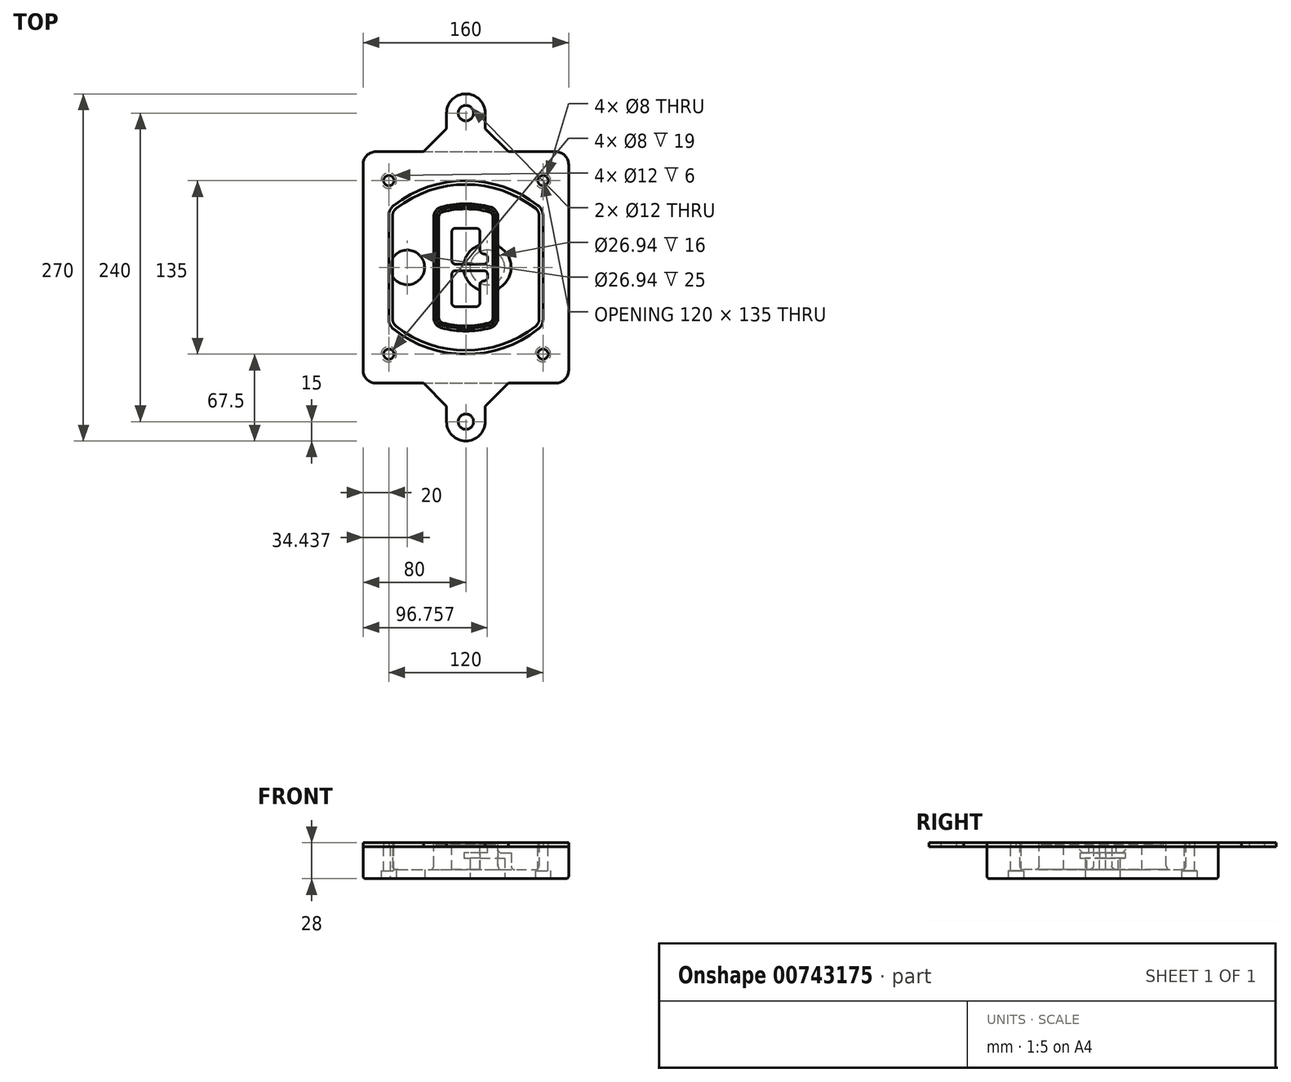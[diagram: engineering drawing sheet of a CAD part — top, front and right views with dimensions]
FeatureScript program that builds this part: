
annotation { "Feature Type Name" : "Feature", "Feature Type Description" : "" }
export const myFeature = defineFeature(function(context is Context, id is Id, definition is map)
    precondition{}
    {
        {
            var Q0;
            Q0=qCreatedBy(makeId("Top.planeOp"),FACE);
            var sketch = newSketch(context, id + "F0", { "sketchPlane" : qUnion([Q0])});
            skPoint(sketch, "E0.rect.middle", {"position": v(0, 0) * mm});
            skLineSegment(sketch, "E1.bottom", {"start": v(-70, -90) * mm, "end": v(70, -90) * mm});
            skLineSegment(sketch, "E1.top", {"start": v(-70, 90) * mm, "end": v(70, 90) * mm});
            skLineSegment(sketch, "E1.left", {"start": v(-80, -80) * mm, "end": v(-80, 80) * mm});
            skLineSegment(sketch, "E1.right", {"start": v(80, -80) * mm, "end": v(80, 80) * mm});
            skLineSegment(sketch, "E2", {"start": v(-80, 90) * mm, "end": v(80, -90) * mm, "construction": true});
            skLineSegment(sketch, "E3", {"start": v(80, 90) * mm, "end": v(-80, -90) * mm, "construction": true});
            skCircle(sketch, "E4", {"center": v(-60, 67.5) * mm, "radius": 4 * mm});
            skCircle(sketch, "E5", {"center": v(60, 67.5) * mm, "radius": 4 * mm});
            skCircle(sketch, "E6", {"center": v(60, -67.5) * mm, "radius": 4 * mm});
            skCircle(sketch, "E7", {"center": v(-60, -67.5) * mm, "radius": 4 * mm});
            skLineSegment(sketch, "E8", {"start": v(-60, 67.5) * mm, "end": v(60, 67.5) * mm, "construction": true});
            skLineSegment(sketch, "E9", {"start": v(60, 67.5) * mm, "end": v(60, -67.5) * mm, "construction": true});
            skLineSegment(sketch, "E10", {"start": v(60, -67.5) * mm, "end": v(-60, -67.5) * mm, "construction": true});
            skLineSegment(sketch, "E11", {"start": v(-60, -67.5) * mm, "end": v(-60, 67.5) * mm, "construction": true});
            skLineSegment(sketch, "E12", {"start": v(-60, 40.3) * mm, "end": v(-60, -40.3) * mm});
            skLineSegment(sketch, "E13", {"start": v(60, 40.3) * mm, "end": v(60, -40.3) * mm});
            skArc(sketch, "E14", {"start": v(56.15, 48.18) * mm, "mid": v(0, 67.5) * mm, "end": v(-56.15, 48.18) * mm});
            skArc(sketch, "E15", {"start": v(-56.15, -48.18) * mm, "mid": v(0, -67.5) * mm, "end": v(56.15, -48.18) * mm});
            skLineSegment(sketch, "E16", {"start": v(-60, 0) * mm, "end": v(60, 0) * mm, "construction": true});
            skPoint(sketch, "E17.visualSharp", {"position": v(-60, -45) * mm});
            skArc(sketch, "E17.filletArc", {"start": v(-60, -40.3) * mm, "mid": v(-58.99, -44.68) * mm, "end": v(-56.15, -48.18) * mm});
            skPoint(sketch, "E18.visualSharp", {"position": v(-60, 45) * mm});
            skArc(sketch, "E18.filletArc", {"start": v(-56.15, 48.18) * mm, "mid": v(-58.99, 44.68) * mm, "end": v(-60, 40.3) * mm});
            skPoint(sketch, "E19.visualSharp", {"position": v(60, 45) * mm});
            skArc(sketch, "E19.filletArc", {"start": v(60, 40.3) * mm, "mid": v(58.99, 44.68) * mm, "end": v(56.15, 48.18) * mm});
            skPoint(sketch, "E20.visualSharp", {"position": v(60, -45) * mm});
            skArc(sketch, "E20.filletArc", {"start": v(56.15, -48.18) * mm, "mid": v(58.99, -44.68) * mm, "end": v(60, -40.3) * mm});
            skPoint(sketch, "E21.visualSharp", {"position": v(-80, 90) * mm});
            skArc(sketch, "E21.filletArc", {"start": v(-70, 90) * mm, "mid": v(-77.07, 87.07) * mm, "end": v(-80, 80) * mm});
            skPoint(sketch, "E22.visualSharp", {"position": v(80, 90) * mm});
            skArc(sketch, "E22.filletArc", {"start": v(80, 80) * mm, "mid": v(77.07, 87.07) * mm, "end": v(70, 90) * mm});
            skPoint(sketch, "E23.visualSharp", {"position": v(80, -90) * mm});
            skArc(sketch, "E23.filletArc", {"start": v(70, -90) * mm, "mid": v(77.07, -87.07) * mm, "end": v(80, -80) * mm});
            skPoint(sketch, "E24.visualSharp", {"position": v(-80, -90) * mm});
            skArc(sketch, "E24.filletArc", {"start": v(-80, -80) * mm, "mid": v(-77.07, -87.07) * mm, "end": v(-70, -90) * mm});
            skArc(sketch, "E25.0", {"start": v(57, 40.3) * mm, "mid": v(56.3, 43.36) * mm, "end": v(54.3, 45.81) * mm});
            skLineSegment(sketch, "E25.1", {"start": v(57, 40.3) * mm, "end": v(57, -40.3) * mm});
            skArc(sketch, "E25.2", {"start": v(54.3, -45.81) * mm, "mid": v(56.3, -43.36) * mm, "end": v(57, -40.3) * mm});
            skArc(sketch, "E25.3", {"start": v(-54.3, -45.81) * mm, "mid": v(0, -64.5) * mm, "end": v(54.3, -45.81) * mm});
            skArc(sketch, "E25.4", {"start": v(-57, -40.3) * mm, "mid": v(-56.3, -43.36) * mm, "end": v(-54.3, -45.81) * mm});
            skArc(sketch, "E25.5", {"start": v(54.3, 45.81) * mm, "mid": v(0, 64.5) * mm, "end": v(-54.3, 45.81) * mm});
            skLineSegment(sketch, "E25.6", {"start": v(-57, 40.3) * mm, "end": v(-57, -40.3) * mm});
            skArc(sketch, "E25.7", {"start": v(-54.3, 45.81) * mm, "mid": v(-56.3, 43.36) * mm, "end": v(-57, 40.3) * mm});
            skArc(sketch, "E26.0", {"start": v(-58.62, 51.33) * mm, "mid": v(-62.58, 46.43) * mm, "end": v(-64, 40.3) * mm});
            skArc(sketch, "E26.1", {"start": v(58.62, 51.33) * mm, "mid": v(0, 71.5) * mm, "end": v(-58.62, 51.33) * mm});
            skArc(sketch, "E26.2", {"start": v(64, 40.3) * mm, "mid": v(62.58, 46.43) * mm, "end": v(58.62, 51.33) * mm});
            skLineSegment(sketch, "E26.3", {"start": v(64, 40.3) * mm, "end": v(64, -40.3) * mm});
            skArc(sketch, "E26.4", {"start": v(58.62, -51.33) * mm, "mid": v(62.58, -46.43) * mm, "end": v(64, -40.3) * mm});
            skLineSegment(sketch, "E26.5", {"start": v(-64, 40.3) * mm, "end": v(-64, -40.3) * mm});
            skArc(sketch, "E26.6", {"start": v(-58.62, -51.33) * mm, "mid": v(0, -71.5) * mm, "end": v(58.62, -51.33) * mm});
            skArc(sketch, "E26.7", {"start": v(-64, -40.3) * mm, "mid": v(-62.58, -46.43) * mm, "end": v(-58.62, -51.33) * mm});
            skSolve(sketch);
        }
        {
            var Q0;
            Q0=makeQuery(id+"F0.imprint","IMPRINT",FACE,{"disambiguationData":[TD([[makeQuery(id+"F0.imprint","IMPRINT",EDGE,{"derivedFrom":sQuery(id+"F0.wireOp",EDGE,"E1.bottom")}),1.0]])]});
            var Q1;
            Q1=makeQuery(id+"F0.imprint","IMPRINT",FACE,{"disambiguationData":[TD([[makeQuery(id+"F0.imprint","IMPRINT",EDGE,{"derivedFrom":sQuery(id+"F0.wireOp",EDGE,"E12")}),1.0]])]});
            var Q2;
            Q2=makeQuery(id+"F0.imprint","IMPRINT",FACE,{"disambiguationData":[TD([[makeQuery(id+"F0.imprint","IMPRINT",EDGE,{"derivedFrom":sQuery(id+"F0.wireOp",EDGE,"E25.0")}),1.0]])]});
            var Q3;
            Q3=makeQuery(id+"F0.imprint","IMPRINT",FACE,{"disambiguationData":[TD([[makeQuery(id+"F0.imprint","IMPRINT",EDGE,{"derivedFrom":sQuery(id+"F0.wireOp",EDGE,"E12")}),-1.0]])]});
            extrude(context, id + "F1", {"entities" : qUnion([Q0, Q1, Q2, Q3]), "oppositeDirection" : true, "depth" : 25 * mm});
        }
        {
            var Q0;
            Q0=makeQuery(id+"F0.imprint","IMPRINT",FACE,{"disambiguationData":[TD([[makeQuery(id+"F0.imprint","IMPRINT",EDGE,{"derivedFrom":sQuery(id+"F0.wireOp",EDGE,"E12")}),1.0]])]});
            extrude(context, id + "F2", {"entities" : qUnion([Q0]), "operationType" : NewBodyOperationType.ADD, "depth" : 3 * mm});
        }
        {
            var Q0;
            Q0=makeQuery(id+"F0.imprint","IMPRINT",FACE,{"disambiguationData":[TD([[makeQuery(id+"F0.imprint","IMPRINT",EDGE,{"derivedFrom":sQuery(id+"F0.wireOp",EDGE,"E25.0")}),1.0]])]});
            extrude(context, id + "F3", {"entities" : qUnion([Q0]), "operationType" : NewBodyOperationType.REMOVE, "oppositeDirection" : true, "depth" : 18 * mm});
        }
        {
            var Q0;
            Q0=makeQuery(id+"F2.opExtrude","CAP_FACE",FACE,{"disambiguationData":[OSD([sQuery(id+"F0.wireOp",EDGE,"E12"),sQuery(id+"F0.wireOp",EDGE,"E13"),sQuery(id+"F0.wireOp",EDGE,"E14"),sQuery(id+"F0.wireOp",EDGE,"E15"),sQuery(id+"F0.wireOp",EDGE,"E17.filletArc"),sQuery(id+"F0.wireOp",EDGE,"E18.filletArc"),sQuery(id+"F0.wireOp",EDGE,"E19.filletArc"),sQuery(id+"F0.wireOp",EDGE,"E20.filletArc"),sQuery(id+"F0.wireOp",EDGE,"E25.0"),sQuery(id+"F0.wireOp",EDGE,"E25.1"),sQuery(id+"F0.wireOp",EDGE,"E25.2"),sQuery(id+"F0.wireOp",EDGE,"E25.3"),sQuery(id+"F0.wireOp",EDGE,"E25.4"),sQuery(id+"F0.wireOp",EDGE,"E25.5"),sQuery(id+"F0.wireOp",EDGE,"E25.6"),sQuery(id+"F0.wireOp",EDGE,"E25.7")])],"isStart":false});
            var sketch = newSketch(context, id + "F4", { "sketchPlane" : qUnion([Q0])});
            skArc(sketch, "E27.0", {"start": v(-19.08, -46.97) * mm, "mid": v(0, -49.5) * mm, "end": v(19.08, -46.97) * mm});
            skArc(sketch, "E28.0", {"start": v(19.08, 46.97) * mm, "mid": v(0, 49.5) * mm, "end": v(-19.08, 46.97) * mm});
            skLineSegment(sketch, "E29", {"start": v(-25, 39.25) * mm, "end": v(-25, -39.25) * mm});
            skLineSegment(sketch, "E30", {"start": v(25, 39.25) * mm, "end": v(25, -39.25) * mm});
            skLineSegment(sketch, "E31", {"start": v(-25, 45.1) * mm, "end": v(25, 45.1) * mm, "construction": true});
            skLineSegment(sketch, "E32", {"start": v(-25, -45.1) * mm, "end": v(25, -45.1) * mm, "construction": true});
            skPoint(sketch, "E33.visualSharp", {"position": v(-25, 45.1) * mm});
            skArc(sketch, "E33.filletArc", {"start": v(-19.08, 46.97) * mm, "mid": v(-23.35, 44.11) * mm, "end": v(-25, 39.25) * mm});
            skPoint(sketch, "E34.visualSharp", {"position": v(25, 45.1) * mm});
            skArc(sketch, "E34.filletArc", {"start": v(25, 39.25) * mm, "mid": v(23.35, 44.11) * mm, "end": v(19.08, 46.97) * mm});
            skPoint(sketch, "E35.visualSharp", {"position": v(25, -45.1) * mm});
            skArc(sketch, "E35.filletArc", {"start": v(19.08, -46.97) * mm, "mid": v(23.35, -44.11) * mm, "end": v(25, -39.25) * mm});
            skPoint(sketch, "E36.visualSharp", {"position": v(-25, -45.1) * mm});
            skArc(sketch, "E36.filletArc", {"start": v(-25, -39.25) * mm, "mid": v(-23.35, -44.11) * mm, "end": v(-19.08, -46.97) * mm});
            skArc(sketch, "E37.0", {"start": v(54.3, 45.81) * mm, "mid": v(0, 64.5) * mm, "end": v(-54.3, 45.81) * mm});
            skArc(sketch, "E37.1", {"start": v(-54.3, 45.81) * mm, "mid": v(-56.3, 43.36) * mm, "end": v(-57, 40.3) * mm});
            skLineSegment(sketch, "E37.2", {"start": v(-57, 40.3) * mm, "end": v(-57, -40.3) * mm});
            skArc(sketch, "E37.3", {"start": v(-57, -40.3) * mm, "mid": v(-56.3, -43.36) * mm, "end": v(-54.3, -45.81) * mm});
            skArc(sketch, "E37.4", {"start": v(-54.3, -45.81) * mm, "mid": v(0, -64.5) * mm, "end": v(54.3, -45.81) * mm});
            skArc(sketch, "E37.5", {"start": v(54.3, -45.81) * mm, "mid": v(56.3, -43.36) * mm, "end": v(57, -40.3) * mm});
            skLineSegment(sketch, "E37.6", {"start": v(57, 40.3) * mm, "end": v(57, -40.3) * mm});
            skArc(sketch, "E37.7", {"start": v(57, 40.3) * mm, "mid": v(56.3, 43.36) * mm, "end": v(54.3, 45.81) * mm});
            skLineSegment(sketch, "E38.0", {"start": v(23, 39.25) * mm, "end": v(23, -39.25) * mm});
            skArc(sketch, "E38.1", {"start": v(18.56, -45.04) * mm, "mid": v(21.76, -42.9) * mm, "end": v(23, -39.25) * mm});
            skArc(sketch, "E38.2", {"start": v(-18.56, -45.04) * mm, "mid": v(0, -47.5) * mm, "end": v(18.56, -45.04) * mm});
            skArc(sketch, "E38.3", {"start": v(-23, -39.25) * mm, "mid": v(-21.76, -42.9) * mm, "end": v(-18.56, -45.04) * mm});
            skLineSegment(sketch, "E38.4", {"start": v(-23, 39.25) * mm, "end": v(-23, -39.25) * mm});
            skArc(sketch, "E38.5", {"start": v(23, 39.25) * mm, "mid": v(21.76, 42.9) * mm, "end": v(18.56, 45.04) * mm});
            skArc(sketch, "E38.6", {"start": v(-18.56, 45.04) * mm, "mid": v(-21.76, 42.9) * mm, "end": v(-23, 39.25) * mm});
            skArc(sketch, "E38.7", {"start": v(18.56, 45.04) * mm, "mid": v(0, 47.5) * mm, "end": v(-18.56, 45.04) * mm});
            skArc(sketch, "E39.0", {"start": v(21, 39.25) * mm, "mid": v(20.18, 41.68) * mm, "end": v(18.04, 43.1) * mm});
            skLineSegment(sketch, "E39.1", {"start": v(21, 39.25) * mm, "end": v(21, -39.25) * mm});
            skArc(sketch, "E39.2", {"start": v(18.04, -43.1) * mm, "mid": v(20.18, -41.68) * mm, "end": v(21, -39.25) * mm});
            skArc(sketch, "E39.3", {"start": v(-18.04, -43.1) * mm, "mid": v(0, -45.5) * mm, "end": v(18.04, -43.1) * mm});
            skArc(sketch, "E39.4", {"start": v(-21, -39.25) * mm, "mid": v(-20.18, -41.68) * mm, "end": v(-18.04, -43.1) * mm});
            skArc(sketch, "E39.5", {"start": v(18.04, 43.1) * mm, "mid": v(0, 45.5) * mm, "end": v(-18.04, 43.1) * mm});
            skLineSegment(sketch, "E39.6", {"start": v(-21, 39.25) * mm, "end": v(-21, -39.25) * mm});
            skArc(sketch, "E39.7", {"start": v(-18.04, 43.1) * mm, "mid": v(-20.18, 41.68) * mm, "end": v(-21, 39.25) * mm});
            skLineSegment(sketch, "E40", {"start": v(-25, 0) * mm, "end": v(25, 0) * mm, "construction": true});
            skLineSegment(sketch, "E41", {"start": v(-11, 5.5) * mm, "end": v(-11, 27.5) * mm});
            skLineSegment(sketch, "E42", {"start": v(-8, 30.5) * mm, "end": v(8, 30.5) * mm});
            skLineSegment(sketch, "E43", {"start": v(11, 27.5) * mm, "end": v(11, 13.5) * mm});
            skLineSegment(sketch, "E44", {"start": v(14, 10.5) * mm, "end": v(14, 10.5) * mm});
            skLineSegment(sketch, "E45", {"start": v(17, 7.5) * mm, "end": v(17, 5.5) * mm});
            skLineSegment(sketch, "E46", {"start": v(14, 2.5) * mm, "end": v(-8, 2.5) * mm});
            skPoint(sketch, "E47.visualSharp", {"position": v(-11, 30.5) * mm});
            skArc(sketch, "E47.filletArc", {"start": v(-8, 30.5) * mm, "mid": v(-10.12, 29.62) * mm, "end": v(-11, 27.5) * mm});
            skPoint(sketch, "E48.visualSharp", {"position": v(11, 30.5) * mm});
            skArc(sketch, "E48.filletArc", {"start": v(11, 27.5) * mm, "mid": v(10.12, 29.62) * mm, "end": v(8, 30.5) * mm});
            skPoint(sketch, "E49.visualSharp", {"position": v(11, 10.5) * mm});
            skArc(sketch, "E49.filletArc", {"start": v(11, 13.5) * mm, "mid": v(11.88, 11.38) * mm, "end": v(14, 10.5) * mm});
            skPoint(sketch, "E50.visualSharp", {"position": v(17, 10.5) * mm});
            skArc(sketch, "E50.filletArc", {"start": v(17, 7.5) * mm, "mid": v(16.12, 9.62) * mm, "end": v(14, 10.5) * mm});
            skPoint(sketch, "E51.visualSharp", {"position": v(17, 2.5) * mm});
            skArc(sketch, "E51.filletArc", {"start": v(14, 2.5) * mm, "mid": v(16.12, 3.38) * mm, "end": v(17, 5.5) * mm});
            skPoint(sketch, "E52.visualSharp", {"position": v(-11, 2.5) * mm});
            skArc(sketch, "E52.filletArc", {"start": v(-11, 5.5) * mm, "mid": v(-10.12, 3.38) * mm, "end": v(-8, 2.5) * mm});
            skLineSegment(sketch, "E53.0.MirrorCS", {"start": v(14, -2.5) * mm, "end": v(-8, -2.5) * mm});
            skArc(sketch, "E54.0.MirrorCS", {"start": v(-11, -5.5) * mm, "mid": v(-10.12, -3.38) * mm, "end": v(-8, -2.5) * mm});
            skLineSegment(sketch, "E55.0.MirrorCS", {"start": v(-11, -5.5) * mm, "end": v(-11, -27.5) * mm});
            skArc(sketch, "E56.0.MirrorCS", {"start": v(-8, -30.5) * mm, "mid": v(-10.12, -29.62) * mm, "end": v(-11, -27.5) * mm});
            skLineSegment(sketch, "E57.0.MirrorCS", {"start": v(-8, -30.5) * mm, "end": v(8, -30.5) * mm});
            skArc(sketch, "E58.0.MirrorCS", {"start": v(11, -27.5) * mm, "mid": v(10.12, -29.62) * mm, "end": v(8, -30.5) * mm});
            skLineSegment(sketch, "E59.0.MirrorCS", {"start": v(11, -27.5) * mm, "end": v(11, -13.5) * mm});
            skArc(sketch, "E60.0.MirrorCS", {"start": v(11, -13.5) * mm, "mid": v(11.88, -11.38) * mm, "end": v(14, -10.5) * mm});
            skArc(sketch, "E61.0.MirrorCS", {"start": v(17, -7.5) * mm, "mid": v(16.12, -9.62) * mm, "end": v(14, -10.5) * mm});
            skLineSegment(sketch, "E62.0.MirrorCS", {"start": v(17, -7.5) * mm, "end": v(17, -5.5) * mm});
            skArc(sketch, "E63.0.MirrorCS", {"start": v(14, -2.5) * mm, "mid": v(16.12, -3.38) * mm, "end": v(17, -5.5) * mm});
            skSolve(sketch);
        }
        {
            var Q0;
            Q0=makeQuery(id+"F4.imprint","IMPRINT",FACE,{"disambiguationData":[TD([[makeQuery(id+"F4.imprint","IMPRINT",EDGE,{"derivedFrom":sQuery(id+"F4.wireOp",EDGE,"E27.0")}),1.0]])]});
            var Q1;
            Q1=makeQuery(id+"F4.imprint","IMPRINT",FACE,{"disambiguationData":[TD([[makeQuery(id+"F4.imprint","IMPRINT",EDGE,{"derivedFrom":sQuery(id+"F4.wireOp",EDGE,"E38.0")}),-1.0]])]});
            var Q2;
            Q2=makeQuery(id+"F4.imprint","IMPRINT",FACE,{"disambiguationData":[TD([[makeQuery(id+"F4.imprint","IMPRINT",EDGE,{"derivedFrom":sQuery(id+"F4.wireOp",EDGE,"E39.0")}),1.0]])]});
            extrude(context, id + "F5", {"entities" : qUnion([Q0, Q1, Q2]), "operationType" : NewBodyOperationType.ADD, "endBound" : BoundingType.UP_TO_NEXT, "oppositeDirection" : true, "depth" : 25 * mm});
        }
        {
            var Q0;
            Q0=makeQuery(id+"F4.imprint","IMPRINT",FACE,{"disambiguationData":[TD([[makeQuery(id+"F4.imprint","IMPRINT",EDGE,{"derivedFrom":sQuery(id+"F4.wireOp",EDGE,"E38.0")}),-1.0]])]});
            extrude(context, id + "F6", {"entities" : qUnion([Q0]), "operationType" : NewBodyOperationType.REMOVE, "oppositeDirection" : true, "depth" : 2 * mm});
        }
        {
            var Q0;
            Q0=makeQuery(id+"F1.opExtrude","CAP_FACE",FACE,{"disambiguationData":[OSD([sQuery(id+"F0.wireOp",EDGE,"E1.bottom"),sQuery(id+"F0.wireOp",EDGE,"E1.top"),sQuery(id+"F0.wireOp",EDGE,"E1.left"),sQuery(id+"F0.wireOp",EDGE,"E1.right"),sQuery(id+"F0.wireOp",EDGE,"E4"),sQuery(id+"F0.wireOp",EDGE,"E5"),sQuery(id+"F0.wireOp",EDGE,"E6"),sQuery(id+"F0.wireOp",EDGE,"E7"),sQuery(id+"F0.wireOp",EDGE,"E21.filletArc"),sQuery(id+"F0.wireOp",EDGE,"E22.filletArc"),sQuery(id+"F0.wireOp",EDGE,"E23.filletArc"),sQuery(id+"F0.wireOp",EDGE,"E24.filletArc")])],"isStart":false});
            var sketch = newSketch(context, id + "F7", { "sketchPlane" : qUnion([Q0])});
            skCircle(sketch, "E64", {"center": v(16.76, 0) * mm, "radius": 13.47 * mm});
            skCircle(sketch, "E65", {"center": v(-45.56, 0) * mm, "radius": 13.47 * mm});
            skLineSegment(sketch, "E66", {"start": v(80, 0) * mm, "end": v(-80, 0) * mm});
            skCircle(sketch, "E67", {"center": v(16.76, 0) * mm, "radius": 18.47 * mm});
            skCircle(sketch, "E68", {"center": v(60, -67.5) * mm, "radius": 6 * mm});
            skCircle(sketch, "E69", {"center": v(-60, -67.5) * mm, "radius": 6 * mm});
            skCircle(sketch, "E70", {"center": v(-60, 67.5) * mm, "radius": 6 * mm});
            skCircle(sketch, "E71", {"center": v(60, 67.5) * mm, "radius": 6 * mm});
            skSolve(sketch);
        }
        {
            var Q0;
            {var subQ1=sQuery(id+"F7.wireOp",EDGE,"E66");var subQ4=sQuery(id+"F7.wireOp",EDGE,"E64");var subQ6=makeQuery(id+"F7.imprint","INTERSECT",VERTEX,{"disambiguationData":[OD(0.0)],"derivedFrom":[subQ4,subQ1]});Q0=makeQuery(id+"F7.imprint","IMPRINT",FACE,{"disambiguationData":[TD([[makeQuery(id+"F7.imprint","IMPRINT",EDGE,{"disambiguationData":[TD([[subQ6,-1.0]])],"derivedFrom":subQ4}),-1.0]])]});}
            var Q1;
            {var subQ0=sQuery(id+"F7.wireOp",EDGE,"E66");var subQ1=sQuery(id+"F7.wireOp",EDGE,"E64");var subQ3=makeQuery(id+"F7.imprint","INTERSECT",VERTEX,{"disambiguationData":[OD(0.0)],"derivedFrom":[subQ1,subQ0]});Q1=makeQuery(id+"F7.imprint","IMPRINT",FACE,{"disambiguationData":[TD([[makeQuery(id+"F7.imprint","IMPRINT",EDGE,{"disambiguationData":[TD([[subQ3,-1.0]])],"derivedFrom":subQ1}),1.0]])]});}
            var Q2;
            {var subQ0=sQuery(id+"F7.wireOp",EDGE,"E66");var subQ1=sQuery(id+"F7.wireOp",EDGE,"E64");var subQ3=makeQuery(id+"F7.imprint","INTERSECT",VERTEX,{"disambiguationData":[OD(0.0)],"derivedFrom":[subQ1,subQ0]});Q2=makeQuery(id+"F7.imprint","IMPRINT",FACE,{"disambiguationData":[TD([[makeQuery(id+"F7.imprint","IMPRINT",EDGE,{"disambiguationData":[TD([[subQ3,1.0]])],"derivedFrom":subQ1}),1.0]])]});}
            var Q3;
            {var subQ1=sQuery(id+"F7.wireOp",EDGE,"E66");var subQ4=sQuery(id+"F7.wireOp",EDGE,"E64");var subQ6=makeQuery(id+"F7.imprint","INTERSECT",VERTEX,{"disambiguationData":[OD(0.0)],"derivedFrom":[subQ4,subQ1]});Q3=makeQuery(id+"F7.imprint","IMPRINT",FACE,{"disambiguationData":[TD([[makeQuery(id+"F7.imprint","IMPRINT",EDGE,{"disambiguationData":[TD([[subQ6,1.0]])],"derivedFrom":subQ4}),-1.0]])]});}
            extrude(context, id + "F8", {"entities" : qUnion([Q0, Q1, Q2, Q3]), "operationType" : NewBodyOperationType.ADD, "oppositeDirection" : true, "depth" : 20 * mm});
        }
        {
            var Q0;
            {var subQ0=sQuery(id+"F7.wireOp",EDGE,"E66");var subQ1=sQuery(id+"F7.wireOp",EDGE,"E64");var subQ3=makeQuery(id+"F7.imprint","INTERSECT",VERTEX,{"disambiguationData":[OD(0.0)],"derivedFrom":[subQ1,subQ0]});Q0=makeQuery(id+"F7.imprint","IMPRINT",FACE,{"disambiguationData":[TD([[makeQuery(id+"F7.imprint","IMPRINT",EDGE,{"disambiguationData":[TD([[subQ3,-1.0]])],"derivedFrom":subQ1}),1.0]])]});}
            var Q1;
            {var subQ0=sQuery(id+"F7.wireOp",EDGE,"E66");var subQ1=sQuery(id+"F7.wireOp",EDGE,"E64");var subQ3=makeQuery(id+"F7.imprint","INTERSECT",VERTEX,{"disambiguationData":[OD(0.0)],"derivedFrom":[subQ1,subQ0]});Q1=makeQuery(id+"F7.imprint","IMPRINT",FACE,{"disambiguationData":[TD([[makeQuery(id+"F7.imprint","IMPRINT",EDGE,{"disambiguationData":[TD([[subQ3,1.0]])],"derivedFrom":subQ1}),1.0]])]});}
            extrude(context, id + "F9", {"entities" : qUnion([Q0, Q1]), "operationType" : NewBodyOperationType.REMOVE, "oppositeDirection" : true, "depth" : 16 * mm});
        }
        {
            var Q0;
            {var subQ0=sQuery(id+"F7.wireOp",EDGE,"E66");var subQ1=sQuery(id+"F7.wireOp",EDGE,"E65");var subQ3=makeQuery(id+"F7.imprint","INTERSECT",VERTEX,{"disambiguationData":[OD(0.0)],"derivedFrom":[subQ1,subQ0]});Q0=makeQuery(id+"F7.imprint","IMPRINT",FACE,{"disambiguationData":[TD([[makeQuery(id+"F7.imprint","IMPRINT",EDGE,{"disambiguationData":[TD([[subQ3,-1.0]])],"derivedFrom":subQ1}),1.0]])]});}
            var Q1;
            {var subQ0=sQuery(id+"F7.wireOp",EDGE,"E66");var subQ1=sQuery(id+"F7.wireOp",EDGE,"E65");var subQ3=makeQuery(id+"F7.imprint","INTERSECT",VERTEX,{"disambiguationData":[OD(0.0)],"derivedFrom":[subQ1,subQ0]});Q1=makeQuery(id+"F7.imprint","IMPRINT",FACE,{"disambiguationData":[TD([[makeQuery(id+"F7.imprint","IMPRINT",EDGE,{"disambiguationData":[TD([[subQ3,1.0]])],"derivedFrom":subQ1}),1.0]])]});}
            extrude(context, id + "F10", {"entities" : qUnion([Q0, Q1]), "operationType" : NewBodyOperationType.REMOVE, "oppositeDirection" : true, "depth" : 25 * mm});
        }
        {
            var Q0;
            Q0=makeQuery(id+"F7.imprint","IMPRINT",FACE,{"disambiguationData":[TD([[makeQuery(id+"F7.imprint","IMPRINT",EDGE,{"derivedFrom":sQuery(id+"F7.wireOp",EDGE,"E68")}),1.0]])]});
            var Q1;
            Q1=makeQuery(id+"F7.imprint","IMPRINT",FACE,{"disambiguationData":[TD([[makeQuery(id+"F7.imprint","IMPRINT",EDGE,{"derivedFrom":makeQuery(id+"F1.opExtrude","CAP_EDGE",EDGE,{"disambiguationData":[OSD([sQuery(id+"F0.wireOp",EDGE,"E5")])],"isStart":false})}),-1.0]])]});
            var Q2;
            Q2=makeQuery(id+"F7.imprint","IMPRINT",FACE,{"disambiguationData":[TD([[makeQuery(id+"F7.imprint","IMPRINT",EDGE,{"derivedFrom":sQuery(id+"F7.wireOp",EDGE,"E69")}),1.0]])]});
            var Q3;
            Q3=makeQuery(id+"F7.imprint","IMPRINT",FACE,{"disambiguationData":[TD([[makeQuery(id+"F7.imprint","IMPRINT",EDGE,{"derivedFrom":makeQuery(id+"F1.opExtrude","CAP_EDGE",EDGE,{"disambiguationData":[OSD([sQuery(id+"F0.wireOp",EDGE,"E4")])],"isStart":false})}),-1.0]])]});
            var Q4;
            Q4=makeQuery(id+"F7.imprint","IMPRINT",FACE,{"disambiguationData":[TD([[makeQuery(id+"F7.imprint","IMPRINT",EDGE,{"derivedFrom":sQuery(id+"F7.wireOp",EDGE,"E70")}),1.0]])]});
            var Q5;
            Q5=makeQuery(id+"F7.imprint","IMPRINT",FACE,{"disambiguationData":[TD([[makeQuery(id+"F7.imprint","IMPRINT",EDGE,{"derivedFrom":makeQuery(id+"F1.opExtrude","CAP_EDGE",EDGE,{"disambiguationData":[OSD([sQuery(id+"F0.wireOp",EDGE,"E7")])],"isStart":false})}),-1.0]])]});
            var Q6;
            Q6=makeQuery(id+"F7.imprint","IMPRINT",FACE,{"disambiguationData":[TD([[makeQuery(id+"F7.imprint","IMPRINT",EDGE,{"derivedFrom":sQuery(id+"F7.wireOp",EDGE,"E71")}),1.0]])]});
            var Q7;
            Q7=makeQuery(id+"F7.imprint","IMPRINT",FACE,{"disambiguationData":[TD([[makeQuery(id+"F7.imprint","IMPRINT",EDGE,{"derivedFrom":makeQuery(id+"F1.opExtrude","CAP_EDGE",EDGE,{"disambiguationData":[OSD([sQuery(id+"F0.wireOp",EDGE,"E6")])],"isStart":false})}),-1.0]])]});
            extrude(context, id + "F11", {"entities" : qUnion([Q0, Q1, Q2, Q3, Q4, Q5, Q6, Q7]), "operationType" : NewBodyOperationType.REMOVE, "oppositeDirection" : true, "depth" : 6 * mm});
        }
        {
            var Q0;
            Q0=makeQuery(id+"F9.boolean.opBoolean","COPY",FACE,{"derivedFrom":makeQuery(id+"F9.opExtrude","CAP_FACE",FACE,{"disambiguationData":[OSD([sQuery(id+"F7.wireOp",EDGE,"E64")])],"isStart":false})});
            var sketch = newSketch(context, id + "F12", { "sketchPlane" : qUnion([Q0])});
            skArc(sketch, "E72.0", {"start": v(11, 17.55) * mm, "mid": v(2.57, 11.82) * mm, "end": v(-1.54, 2.5) * mm});
            skArc(sketch, "E72.1", {"start": v(-1.54, -2.5) * mm, "mid": v(2.57, -11.82) * mm, "end": v(11, -17.55) * mm});
            skLineSegment(sketch, "E73", {"start": v(-1.54, -2.5) * mm, "end": v(14, -2.5) * mm});
            skLineSegment(sketch, "E74.0", {"start": v(14, 2.5) * mm, "end": v(-1.54, 2.5) * mm});
            skArc(sketch, "E74.1", {"start": v(14, 2.5) * mm, "mid": v(16.12, 3.38) * mm, "end": v(17, 5.5) * mm});
            skLineSegment(sketch, "E74.2", {"start": v(17, 7.5) * mm, "end": v(17, 5.5) * mm});
            skArc(sketch, "E74.3", {"start": v(17, 7.5) * mm, "mid": v(16.12, 9.62) * mm, "end": v(14, 10.5) * mm});
            skArc(sketch, "E74.4", {"start": v(11, 13.5) * mm, "mid": v(11.88, 11.38) * mm, "end": v(14, 10.5) * mm});
            skLineSegment(sketch, "E74.5", {"start": v(11, 17.55) * mm, "end": v(11, 13.5) * mm});
            skLineSegment(sketch, "E74.7", {"start": v(14, -2.5) * mm, "end": v(-1.54, -2.5) * mm});
            skArc(sketch, "E74.8", {"start": v(14, -2.5) * mm, "mid": v(16.12, -3.38) * mm, "end": v(17, -5.5) * mm});
            skLineSegment(sketch, "E74.9", {"start": v(17, -7.5) * mm, "end": v(17, -5.5) * mm});
            skArc(sketch, "E74.10", {"start": v(17, -7.5) * mm, "mid": v(16.12, -9.62) * mm, "end": v(14, -10.5) * mm});
            skArc(sketch, "E74.11", {"start": v(11, -13.5) * mm, "mid": v(11.88, -11.38) * mm, "end": v(14, -10.5) * mm});
            skLineSegment(sketch, "E74.12", {"start": v(11, -17.55) * mm, "end": v(11, -13.5) * mm});
            skPoint(sketch, "E75.orphan", {"position": v(11, -27.5) * mm});
            skPoint(sketch, "E76.orphan", {"position": v(-8, -2.5) * mm});
            skPoint(sketch, "E77.orphan", {"position": v(-8, 2.5) * mm});
            skPoint(sketch, "E78.orphan", {"position": v(11, 27.5) * mm});
            skSolve(sketch);
        }
        {
            var Q0;
            {var subQ7=sQuery(id+"F12.wireOp",EDGE,"E72.0");var subQ14=sQuery(id+"F12.wireOp",EDGE,"E72.1");var subQ16=sQuery(id+"F12.wireOp",EDGE,"E74.1");var subQ18=sQuery(id+"F12.wireOp",EDGE,"E74.8");Q0=qUnion([makeQuery(id+"F12.imprint","IMPRINT",FACE,{"disambiguationData":[TD([[makeQuery(id+"F12.imprint","IMPRINT",EDGE,{"derivedFrom":subQ7}),1.0]])]}),makeQuery(id+"F12.imprint","IMPRINT",FACE,{"disambiguationData":[TD([[makeQuery(id+"F12.imprint","IMPRINT",EDGE,{"derivedFrom":subQ14}),1.0]])]}),makeQuery(id+"F12.imprint","IMPRINT",FACE,{"disambiguationData":[TD([[makeQuery(id+"F12.imprint","IMPRINT",EDGE,{"derivedFrom":subQ16}),1.0]])]}),makeQuery(id+"F12.imprint","IMPRINT",FACE,{"disambiguationData":[TD([[makeQuery(id+"F12.imprint","IMPRINT",EDGE,{"derivedFrom":subQ18}),-1.0]])]})]);}
            var Q1;
            Q1=makeQuery(id+"F5.boolean.opBoolean","SPLIT",FACE,{"disambiguationData":[TD([makeQuery(id+"F5.opExtrude","SWEPT_FACE",FACE,{"disambiguationData":[OSD([sQuery(id+"F4.wireOp",EDGE,"E41")])]})])],"derivedFrom":makeQuery(id+"F3.boolean.opBoolean","COPY",FACE,{"derivedFrom":makeQuery(id+"F3.opExtrude","CAP_FACE",FACE,{"disambiguationData":[OSD([sQuery(id+"F0.wireOp",EDGE,"E25.0"),sQuery(id+"F0.wireOp",EDGE,"E25.1"),sQuery(id+"F0.wireOp",EDGE,"E25.2"),sQuery(id+"F0.wireOp",EDGE,"E25.3"),sQuery(id+"F0.wireOp",EDGE,"E25.4"),sQuery(id+"F0.wireOp",EDGE,"E25.5"),sQuery(id+"F0.wireOp",EDGE,"E25.6"),sQuery(id+"F0.wireOp",EDGE,"E25.7")])],"isStart":false})})});
            extrude(context, id + "F13", {"entities" : qUnion([Q0]), "operationType" : NewBodyOperationType.REMOVE, "endBound" : BoundingType.UP_TO_SURFACE, "endBoundEntityFace" : qUnion([Q1]), "depth" : 25 * mm});
        }
        {
            var Q0;
            Q0=makeQuery(id+"F3.boolean.opBoolean","COPY",EDGE,{"derivedFrom":makeQuery(id+"F3.opExtrude","CAP_EDGE",EDGE,{"disambiguationData":[OSD([sQuery(id+"F0.wireOp",EDGE,"E25.6")])],"isStart":false})});
            var Q1;
            Q1=makeQuery(id+"F8.boolean.opBoolean","INTERSECT",EDGE,{"derivedFrom":[makeQuery(id+"F5.opExtrude","SWEPT_FACE",FACE,{"disambiguationData":[OSD([sQuery(id+"F4.wireOp",EDGE,"E30")])]}),makeQuery(id+"F8.opExtrude","CAP_FACE",FACE,{"disambiguationData":[OSD([sQuery(id+"F7.wireOp",EDGE,"E67")])],"isStart":false})]});
            var Q2;
            Q2=makeQuery(id+"F8.boolean.opBoolean","INTERSECT",EDGE,{"disambiguationData":[OD(1.0)],"derivedFrom":[makeQuery(id+"F5.opExtrude","SWEPT_FACE",FACE,{"disambiguationData":[OSD([sQuery(id+"F4.wireOp",EDGE,"E30")])]}),makeQuery(id+"F8.opExtrude","SWEPT_FACE",FACE,{"disambiguationData":[OSD([sQuery(id+"F7.wireOp",EDGE,"E67")])]})]});
            var Q3;
            {var subQ0=sQuery(id+"F4.wireOp",EDGE,"E30");Q3=makeQuery(id+"F8.boolean.opBoolean","SPLIT",EDGE,{"disambiguationData":[TD([makeQuery(id+"F5.opExtrude","SWEPT_FACE",FACE,{"disambiguationData":[OSD([sQuery(id+"F4.wireOp",EDGE,"E35.filletArc")])]})])],"derivedFrom":makeQuery(id+"F5.opExtrude","CAP_EDGE",EDGE,{"disambiguationData":[OSD([subQ0])],"isStart":false})});}
            var Q4;
            {var subQ0=sQuery(id+"F0.wireOp",EDGE,"E25.7");var subQ1=sQuery(id+"F0.wireOp",EDGE,"E25.1");var subQ2=sQuery(id+"F0.wireOp",EDGE,"E25.6");var subQ3=sQuery(id+"F0.wireOp",EDGE,"E25.5");var subQ4=sQuery(id+"F0.wireOp",EDGE,"E25.4");var subQ5=sQuery(id+"F0.wireOp",EDGE,"E25.0");var subQ6=sQuery(id+"F0.wireOp",EDGE,"E25.2");var subQ7=sQuery(id+"F0.wireOp",EDGE,"E25.3");Q4=makeQuery(id+"F8.boolean.opBoolean","INTERSECT",EDGE,{"derivedFrom":[makeQuery(id+"F5.boolean.opBoolean","SPLIT",FACE,{"disambiguationData":[TD([makeQuery(id+"F2.opExtrude","SWEPT_FACE",FACE,{"disambiguationData":[OSD([subQ5])]})])],"derivedFrom":makeQuery(id+"F3.boolean.opBoolean","COPY",FACE,{"derivedFrom":makeQuery(id+"F3.opExtrude","CAP_FACE",FACE,{"disambiguationData":[OSD([subQ5,subQ1,subQ6,subQ7,subQ4,subQ3,subQ2,subQ0])],"isStart":false})})}),makeQuery(id+"F8.opExtrude","SWEPT_FACE",FACE,{"disambiguationData":[OSD([sQuery(id+"F7.wireOp",EDGE,"E67")])]})]});}
            var Q5;
            Q5=makeQuery(id+"F8.boolean.opBoolean","INTERSECT",EDGE,{"disambiguationData":[OD(0.0)],"derivedFrom":[makeQuery(id+"F5.opExtrude","SWEPT_FACE",FACE,{"disambiguationData":[OSD([sQuery(id+"F4.wireOp",EDGE,"E30")])]}),makeQuery(id+"F8.opExtrude","SWEPT_FACE",FACE,{"disambiguationData":[OSD([sQuery(id+"F7.wireOp",EDGE,"E67")])]})]});
            fillet(context, id + "F14", {"entities" : qUnion([Q0, Q1, Q2, Q3, Q4, Q5]), "radius" : 3 * mm, "tangentPropagation" : true, "allowEdgeOverflow" : false});
        }
        {
            var Q0;
            Q0=makeQuery(id+"F1.opExtrude","CAP_EDGE",EDGE,{"disambiguationData":[OSD([sQuery(id+"F0.wireOp",EDGE,"E1.bottom")])],"isStart":false});
            fillet(context, id + "F15", {"entities" : qUnion([Q0]), "radius" : 2 * mm, "tangentPropagation" : true, "allowEdgeOverflow" : false});
        }
        {
            var Q0;
            {var subQ0=sQuery(id+"F0.wireOp",EDGE,"E21.filletArc");var subQ1=sQuery(id+"F0.wireOp",EDGE,"E7");var subQ2=sQuery(id+"F0.wireOp",EDGE,"E6");var subQ3=sQuery(id+"F0.wireOp",EDGE,"E5");var subQ4=sQuery(id+"F0.wireOp",EDGE,"E4");var subQ5=sQuery(id+"F0.wireOp",EDGE,"E22.filletArc");var subQ6=sQuery(id+"F0.wireOp",EDGE,"E1.bottom");var subQ7=sQuery(id+"F0.wireOp",EDGE,"E1.right");var subQ8=sQuery(id+"F0.wireOp",EDGE,"E1.top");var subQ9=sQuery(id+"F0.wireOp",EDGE,"E1.left");var subQ10=sQuery(id+"F0.wireOp",EDGE,"E23.filletArc");var subQ11=sQuery(id+"F0.wireOp",EDGE,"E24.filletArc");Q0=makeQuery(id+"F2.boolean.opBoolean","SPLIT",FACE,{"disambiguationData":[TD([makeQuery(id+"F1.opExtrude","SWEPT_FACE",FACE,{"disambiguationData":[OSD([subQ6])]})])],"derivedFrom":makeQuery(id+"F1.opExtrude","CAP_FACE",FACE,{"disambiguationData":[OSD([subQ6,subQ8,subQ9,subQ7,subQ4,subQ3,subQ2,subQ1,subQ0,subQ5,subQ10,subQ11])],"isStart":true})});}
            var sketch = newSketch(context, id + "F16", { "sketchPlane" : qUnion([Q0])});
            skLineSegment(sketch, "E79.0", {"start": v(-70, 90) * mm, "end": v(70, 90) * mm});
            skArc(sketch, "E79.1", {"start": v(-70, 90) * mm, "mid": v(-77.07, 87.07) * mm, "end": v(-80, 80) * mm});
            skLineSegment(sketch, "E79.2", {"start": v(-80, -80) * mm, "end": v(-80, 80) * mm});
            skArc(sketch, "E79.3", {"start": v(80, 80) * mm, "mid": v(77.07, 87.07) * mm, "end": v(70, 90) * mm});
            skLineSegment(sketch, "E79.4", {"start": v(80, -80) * mm, "end": v(80, 80) * mm});
            skArc(sketch, "E79.5", {"start": v(70, -90) * mm, "mid": v(77.07, -87.07) * mm, "end": v(80, -80) * mm});
            skLineSegment(sketch, "E79.6", {"start": v(-70, -90) * mm, "end": v(70, -90) * mm});
            skArc(sketch, "E79.7", {"start": v(-80, -80) * mm, "mid": v(-77.07, -87.07) * mm, "end": v(-70, -90) * mm});
            skCircle(sketch, "E79.8", {"center": v(-60, -67.5) * mm, "radius": 4 * mm});
            skCircle(sketch, "E79.9", {"center": v(-60, 67.5) * mm, "radius": 4 * mm});
            skCircle(sketch, "E79.10", {"center": v(60, 67.5) * mm, "radius": 4 * mm});
            skCircle(sketch, "E79.11", {"center": v(60, -67.5) * mm, "radius": 4 * mm});
            skLineSegment(sketch, "E79.12", {"start": v(60, 40.3) * mm, "end": v(60, -40.3) * mm});
            skArc(sketch, "E79.13", {"start": v(56.15, 48.18) * mm, "mid": v(0, 67.5) * mm, "end": v(-56.15, 48.18) * mm});
            skArc(sketch, "E79.14", {"start": v(60, 40.3) * mm, "mid": v(58.99, 44.68) * mm, "end": v(56.15, 48.18) * mm});
            skArc(sketch, "E79.15", {"start": v(-56.15, 48.18) * mm, "mid": v(-58.99, 44.68) * mm, "end": v(-60, 40.3) * mm});
            skLineSegment(sketch, "E79.16", {"start": v(-60, 40.3) * mm, "end": v(-60, -40.3) * mm});
            skArc(sketch, "E79.17", {"start": v(-60, -40.3) * mm, "mid": v(-58.99, -44.68) * mm, "end": v(-56.15, -48.18) * mm});
            skArc(sketch, "E79.18", {"start": v(-56.15, -48.18) * mm, "mid": v(0, -67.5) * mm, "end": v(56.15, -48.18) * mm});
            skArc(sketch, "E79.19", {"start": v(56.15, -48.18) * mm, "mid": v(58.99, -44.68) * mm, "end": v(60, -40.3) * mm});
            skLineSegment(sketch, "E80", {"start": v(0, 90) * mm, "end": v(0, 120) * mm, "construction": true});
            skCircle(sketch, "E81", {"center": v(0, 120) * mm, "radius": 6 * mm});
            skArc(sketch, "E82", {"start": v(-15, 120) * mm, "mid": v(0, 135) * mm, "end": v(15, 120) * mm});
            skLineSegment(sketch, "E83", {"start": v(-15, 120) * mm, "end": v(-15, 108) * mm});
            skLineSegment(sketch, "E84", {"start": v(15, 120) * mm, "end": v(15, 108) * mm});
            skLineSegment(sketch, "E85", {"start": v(15, 108) * mm, "end": v(33, 90) * mm});
            skLineSegment(sketch, "E86", {"start": v(-15, 108) * mm, "end": v(-33, 90) * mm});
            skLineSegment(sketch, "E87", {"start": v(-80, 0) * mm, "end": v(80, 0) * mm, "construction": true});
            skArc(sketch, "E88.MirrorCS", {"start": v(-15, -120) * mm, "mid": v(0, -135) * mm, "end": v(15, -120) * mm});
            skLineSegment(sketch, "E89.MirrorCS", {"start": v(-15, -120) * mm, "end": v(-15, -108) * mm});
            skLineSegment(sketch, "E90.MirrorCS", {"start": v(15, -120) * mm, "end": v(15, -108) * mm});
            skCircle(sketch, "E91.MirrorC", {"center": v(0, -120) * mm, "radius": 6 * mm});
            skLineSegment(sketch, "E92.MirrorCS", {"start": v(0, -90) * mm, "end": v(0, -120) * mm, "construction": true});
            skLineSegment(sketch, "E93.MirrorCS", {"start": v(-15, -108) * mm, "end": v(-33, -90) * mm});
            skLineSegment(sketch, "E94.MirrorCS", {"start": v(15, -108) * mm, "end": v(33, -90) * mm});
            skSolve(sketch);
        }
        {
            var Q0;
            Q0 = qSketchRegion(id + "F16", true);
            var Q1;
            Q1=makeQuery(id+"F2.opExtrude","CAP_FACE",FACE,{"disambiguationData":[OSD([sQuery(id+"F0.wireOp",EDGE,"E12"),sQuery(id+"F0.wireOp",EDGE,"E13"),sQuery(id+"F0.wireOp",EDGE,"E14"),sQuery(id+"F0.wireOp",EDGE,"E15"),sQuery(id+"F0.wireOp",EDGE,"E17.filletArc"),sQuery(id+"F0.wireOp",EDGE,"E18.filletArc"),sQuery(id+"F0.wireOp",EDGE,"E19.filletArc"),sQuery(id+"F0.wireOp",EDGE,"E20.filletArc"),sQuery(id+"F0.wireOp",EDGE,"E25.0"),sQuery(id+"F0.wireOp",EDGE,"E25.1"),sQuery(id+"F0.wireOp",EDGE,"E25.2"),sQuery(id+"F0.wireOp",EDGE,"E25.3"),sQuery(id+"F0.wireOp",EDGE,"E25.4"),sQuery(id+"F0.wireOp",EDGE,"E25.5"),sQuery(id+"F0.wireOp",EDGE,"E25.6"),sQuery(id+"F0.wireOp",EDGE,"E25.7")])],"isStart":false});
            extrude(context, id + "F17", {"entities" : qUnion([Q0]), "endBound" : BoundingType.UP_TO_SURFACE, "depth" : 25 * mm, "endBoundEntityFace" : qUnion([Q1]), "offsetDistance" : 25 * mm});
        }
    });
